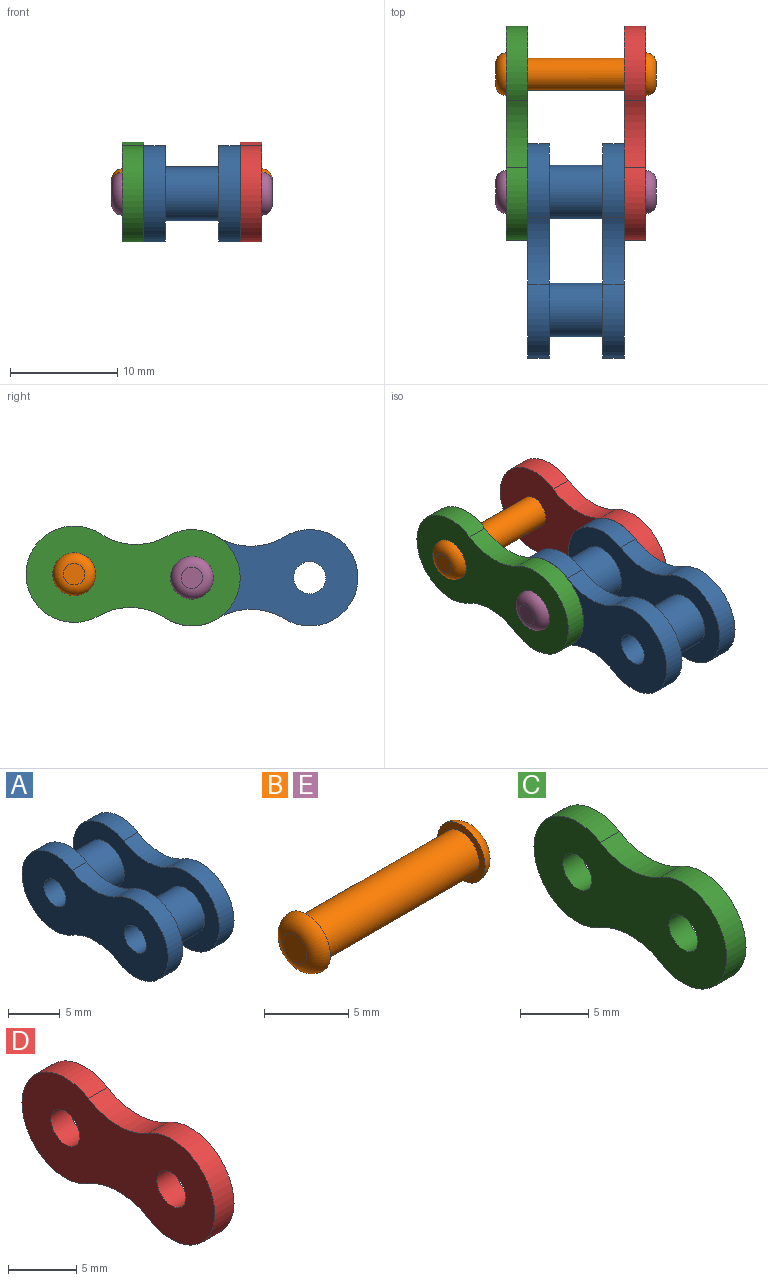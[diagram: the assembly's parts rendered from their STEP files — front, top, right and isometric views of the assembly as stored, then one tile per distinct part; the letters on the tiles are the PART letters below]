
ASSEMBLY  parts=5 mates=5
PART A: 16 faces, bbox 9x20x9 mm
  f0: cylinder r=6mm len=6.29mm, axis (-1,0,0), area 13.2mm2, adj f1,f4,f6,f7
  f1: cylinder r=4.5mm len=9mm, axis (-1,0,0), area 38.2mm2, adj f0,f2,f6,f7
  f2: cylinder r=6mm len=6.29mm, axis (-1,0,0), area 13.2mm2, adj f1,f4,f6,f7
  f3: cylinder r=1.5mm len=9mm, axis (-1,0,0), area 84.8mm2, adj f6,f13
  f4: cylinder r=4.5mm len=9mm, axis (-1,0,0), area 38.2mm2, adj f0,f2,f6,f7
  f5: cylinder r=1.5mm len=9mm, axis (-1,0,0), area 84.8mm2, adj f6,f13
  f6: plane 20x9mm, normal (1,0,0), area 130.5mm2, adj f0,f1,f2,f3,f4,f5
  f7: plane 20x9mm, normal (-1,0,0), area 105.4mm2, adj f0,f1,f2,f4,f14,f15
  f8: plane 20x9mm, normal (1,0,0), area 105.4mm2, adj f9,f10,f11,f12,f14,f15
  f9: cylinder r=6mm len=6.29mm, axis (1,0,0), area 13.2mm2, adj f8,f10,f12,f13
  f10: cylinder r=4.5mm len=9mm, axis (1,0,0), area 38.2mm2, adj f8,f9,f11,f13
  f11: cylinder r=6mm len=6.29mm, axis (1,0,0), area 13.2mm2, adj f8,f10,f12,f13
  f12: cylinder r=4.5mm len=9mm, axis (1,0,0), area 38.2mm2, adj f8,f9,f11,f13
  f13: plane 20x9mm, normal (-1,0,0), area 130.5mm2, adj f3,f5,f9,f10,f11,f12
  f14: cylinder r=2.5mm len=5mm, axis (1,0,0), area 78.5mm2, adj f7,f8
  f15: cylinder r=2.5mm len=5mm, axis (1,0,0), area 78.5mm2, adj f7,f8
PART B: 7 faces, bbox 15x4.3x4.3 mm
  f0: cylinder r=1.5mm len=13mm, axis (-1,0,0), area 122.5mm2, adj f2,f5
  f1: plane 2x2mm, normal (1,0,0), area 3.1mm2, adj f3
  f2: plane 4x4mm, normal (-1,0,0), area 5.5mm2, adj f0,f3
  f3: torus R=1mm, axis (1,0,0), area 16.2mm2, adj f1,f2
  f4: plane 2x2mm, normal (-1,0,0), area 3.1mm2, adj f6
  f5: plane 4x4mm, normal (1,0,0), area 5.5mm2, adj f0,f6
  f6: torus R=1mm, axis (-1,0,0), area 16.2mm2, adj f4,f5
PART C: 8 faces, bbox 2x20x9 mm
  f0: cylinder r=6mm len=6.29mm, axis (1,0,0), area 13.2mm2, adj f1,f4,f6,f7
  f1: cylinder r=4.5mm len=9mm, axis (1,0,0), area 38.2mm2, adj f0,f2,f6,f7
  f2: cylinder r=6mm len=6.29mm, axis (1,0,0), area 13.2mm2, adj f1,f4,f6,f7
  f3: cylinder r=1.5mm len=3mm, axis (1,0,0), area 18.8mm2, adj f6,f7
  f4: cylinder r=4.5mm len=9mm, axis (1,0,0), area 38.2mm2, adj f0,f2,f6,f7
  f5: cylinder r=1.5mm len=3mm, axis (1,0,0), area 18.8mm2, adj f6,f7
  f6: plane 20x9mm, normal (-1,0,0), area 130.5mm2, adj f0,f1,f2,f3,f4,f5
  f7: plane 20x9mm, normal (1,0,0), area 130.5mm2, adj f0,f1,f2,f3,f4,f5
PART D: 8 faces, bbox 2x20x9 mm
  f0: cylinder r=6mm len=6.29mm, axis (-1,0,0), area 13.2mm2, adj f1,f4,f6,f7
  f1: cylinder r=4.5mm len=9mm, axis (-1,0,0), area 38.2mm2, adj f0,f2,f6,f7
  f2: cylinder r=6mm len=6.29mm, axis (-1,0,0), area 13.2mm2, adj f1,f4,f6,f7
  f3: cylinder r=1.5mm len=3mm, axis (-1,0,0), area 18.8mm2, adj f6,f7
  f4: cylinder r=4.5mm len=9mm, axis (-1,0,0), area 38.2mm2, adj f0,f2,f6,f7
  f5: cylinder r=1.5mm len=3mm, axis (-1,0,0), area 18.8mm2, adj f6,f7
  f6: plane 20x9mm, normal (1,0,0), area 130.5mm2, adj f0,f1,f2,f3,f4,f5
  f7: plane 20x9mm, normal (-1,0,0), area 130.5mm2, adj f0,f1,f2,f3,f4,f5
PART E: same geometry as B
PLACE A t=(-8.39,-0.48,6.17)mm
PLACE B rot(axis=(1,0,0),1.7deg) t=(-8.39,16.01,6.5)mm
PLACE C rot(axis=(1,0,0),1.7deg) t=(-8.39,26.1,-15.82)mm
PLACE D rot(axis=(1,0,0),1.7deg) t=(-8.39,26.1,-15.82)mm
PLACE E rot(axis=(-1,0,0),167.6deg) t=(-8.39,5.02,6.17)mm
MATE fastened B.f3 <-> C.f4  axis (1,0,0) through (-14.89,16.01,6.5)mm
MATE fastened B.f0 <-> D.f4  axis (-1,0,0) through (-1.89,16.01,6.5)mm
MATE revolute C.f1 <-> A.f5  axis (1,0,0) through (-12.89,5.02,6.17)mm
MATE cylindrical E.f0 <-> A.f15  axis (-1,0,0) through (-8.39,5.02,6.17)mm
MATE revolute D.f1 <-> A.f5  axis (-1,0,0) through (-3.89,5.02,6.17)mm
